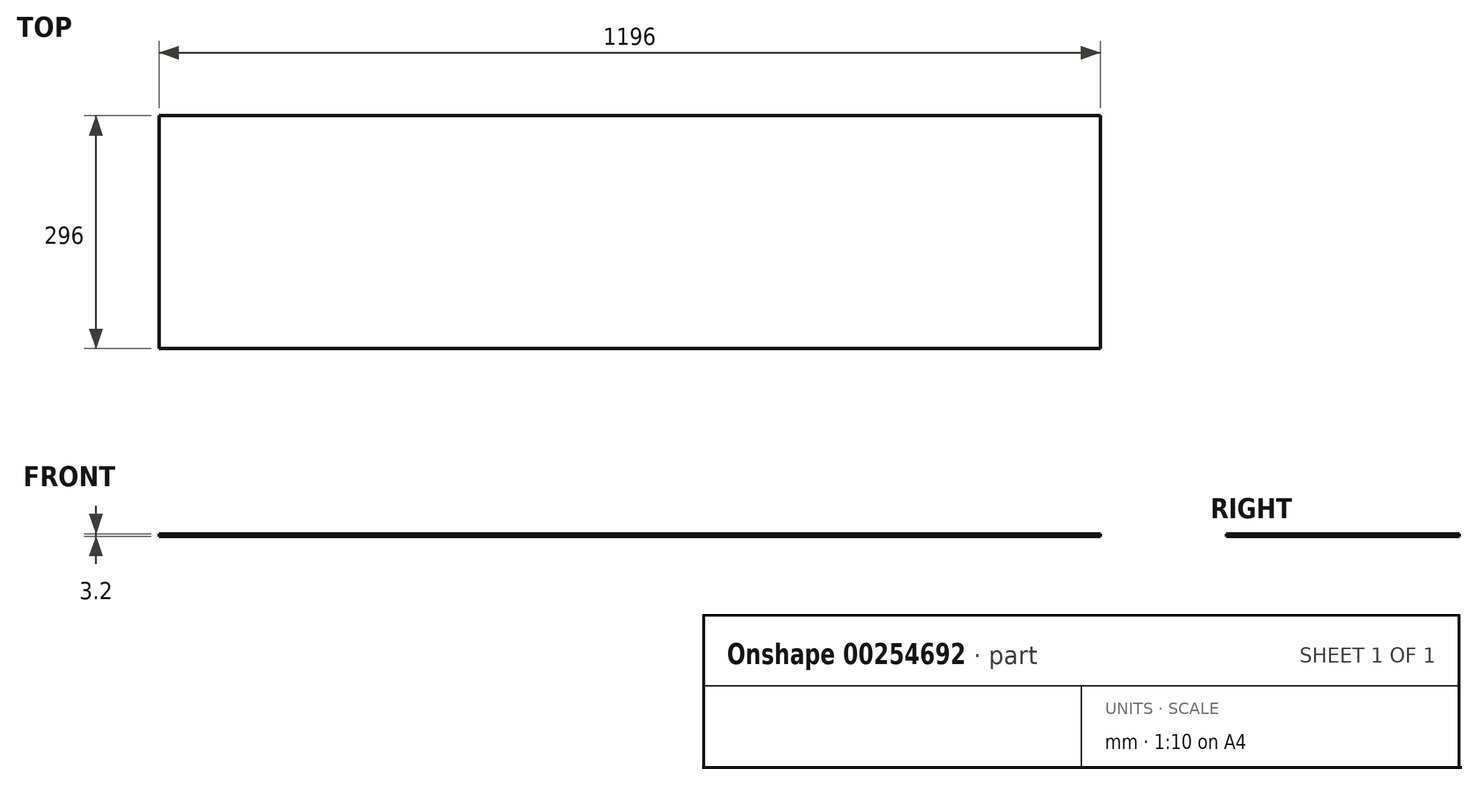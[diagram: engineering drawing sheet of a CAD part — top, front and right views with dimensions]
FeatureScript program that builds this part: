
annotation { "Feature Type Name" : "Feature", "Feature Type Description" : "" }
export const myFeature = defineFeature(function(context is Context, id is Id, definition is map)
    precondition{}
    {
        {
            var Q0;
            Q0=qCreatedBy(makeId("Top.planeOp"),FACE);
            var sketch = newSketch(context, id + "F0", { "sketchPlane" : qUnion([Q0])});
            skLineSegment(sketch, "E0.bottom", {"start": v(0, 0) * mm, "end": v(1196, 0) * mm});
            skLineSegment(sketch, "E0.top", {"start": v(0, 296) * mm, "end": v(1196, 296) * mm});
            skLineSegment(sketch, "E0.left", {"start": v(0, 0) * mm, "end": v(0, 296) * mm});
            skLineSegment(sketch, "E0.right", {"start": v(1196, 0) * mm, "end": v(1196, 296) * mm});
            skSolve(sketch);
        }
        {
            var Q0;
            Q0 = qSketchRegion(id + "F0", true);
            extrude(context, id + "F1", {"entities" : qUnion([Q0]), "depth" : 3.2 * mm});
        }
    });
